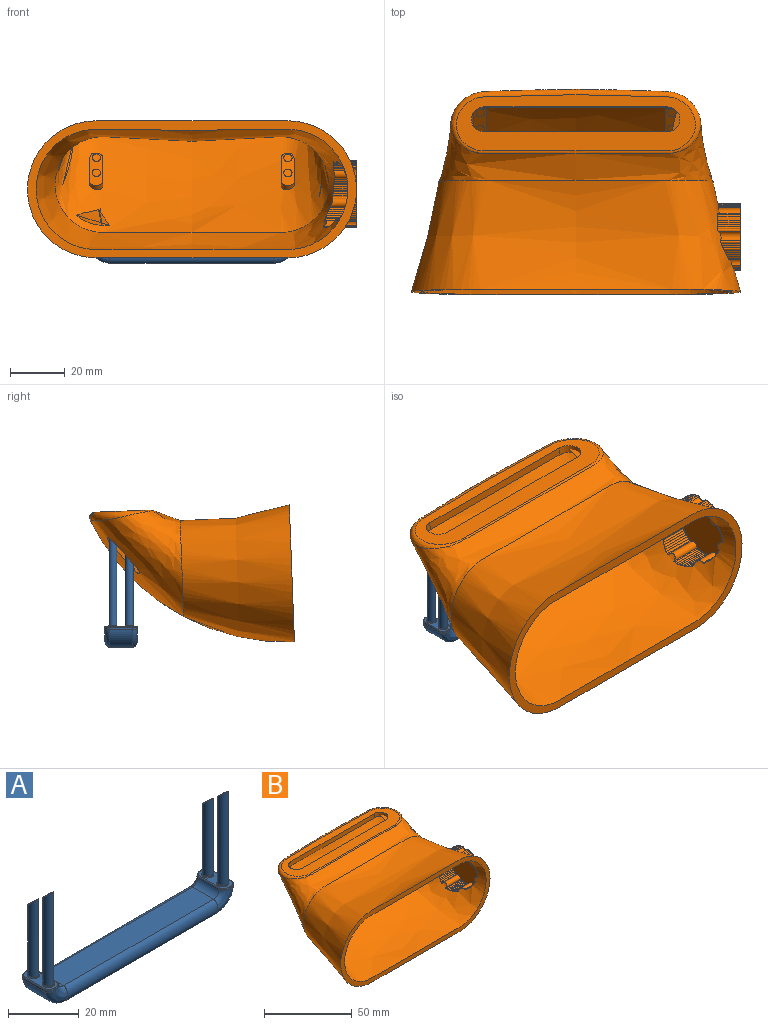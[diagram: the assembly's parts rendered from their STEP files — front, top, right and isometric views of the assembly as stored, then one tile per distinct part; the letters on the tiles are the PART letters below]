
ASSEMBLY  parts=2 mates=1
PART A: 48 faces, bbox 75x15.2x39.8 mm
  f0: cylinder r=1.5mm len=26.61mm, axis (0,0,-1), area 237.6mm2, adj f31,f33
  f1: cylinder r=1.5mm len=32.08mm, axis (0,0,-1), area 289.4mm2, adj f2,f30,f32
  f2: plane 0.1x0mm, normal (0,0,1), area 0mm2, adj f1,f30
  f3: cylinder r=1.5mm len=26.61mm, axis (0,0,-1), area 237.6mm2, adj f29,f41
  f4: cylinder r=1.5mm len=32.08mm, axis (0,0,-1), area 289.4mm2, adj f5,f28,f40
  f5: plane 0.1x0mm, normal (0,0,1), area 0mm2, adj f4,f28
  f6: bspline ~7.5x7.5mm, area 48mm2, adj f9,f10,f13,f23,f25,f37
  f7: bspline ~7.5x7.5mm, area 48mm2, adj f11,f15,f17,f20,f21,f47
  f8: bspline ~7.5x7.5mm, area 48mm2, adj f9,f10,f11,f22,f25,f34
  f9: cylinder r=2.5mm len=8.45mm, axis (0,-1,0), area 31.2mm2, adj f6,f8,f12,f35
  f10: cylinder r=7.5mm len=8.45mm, axis (0,-1,0), area 91mm2, adj f6,f8,f14,f25
  f11: bspline ~60x5mm, area 398.5mm2, adj f7,f8,f12,f14
  f12: plane 60x8.45mm, normal (0,0,1), area 506.7mm2, adj f9,f11,f13,f15
  f13: bspline ~60x5mm, area 398.5mm2, adj f6,f12,f14,f16
  f14: plane 60x8.45mm, normal (0,0,-1), area 506.7mm2, adj f10,f11,f13,f17
  f15: cylinder r=2.5mm len=8.45mm, axis (0,-1,0), area 31.2mm2, adj f7,f12,f16,f45
  f16: bspline ~7.5x7.5mm, area 48mm2, adj f13,f15,f17,f18,f21,f43
  f17: cylinder r=7.5mm len=8.45mm, axis (0,-1,0), area 91mm2, adj f7,f14,f16,f21
  f18: extruded ~2.55x1.69mm, area 2.5mm2, adj f16,f19,f21,f42
  f19: plane 8.45x0.75mm, normal (1,0,0), area 6.3mm2, adj f18,f20,f21,f44
  f20: extruded ~2.55x1.69mm, area 2.5mm2, adj f7,f19,f21,f46
  f21: plane 11.83x2.55mm, normal (0,0,-1), area 0.8mm2, adj f7,f16,f17,f18,f19,f20
  f22: extruded ~2.55x1.69mm, area 2.5mm2, adj f8,f24,f25,f36
  f23: extruded ~2.55x1.69mm, area 2.5mm2, adj f6,f24,f25,f39
  f24: plane 8.45x0.75mm, normal (-1,0,0), area 6.3mm2, adj f22,f23,f25,f38
  f25: plane 11.83x2.55mm, normal (0,0,-1), area 0.8mm2, adj f6,f8,f10,f22,f23,f24
  f26: plane 11.33x4.51mm, normal (0,0,1), area 29mm2, adj f32,f33,f34,f35,f36,f37,f38,f39
  f27: plane 11.33x4.51mm, normal (0,0,1), area 29mm2, adj f40,f41,f42,f43,f44,f45,f46,f47
  f28: plane 3x3mm, normal (0,0.68,0.74), area 9.6mm2, adj f4,f5
  f29: plane 3x3mm, normal (0,0.68,0.74), area 9.6mm2, adj f3
  f30: plane 3x3mm, normal (0,0.68,0.74), area 9.6mm2, adj f1,f2
  f31: plane 3x3mm, normal (0,0.68,0.74), area 9.6mm2, adj f0
  f32: torus R=1.75mm, axis (0,0,-1), area 3.9mm2, adj f1,f26
  f33: torus R=1.75mm, axis (0,0,-1), area 3.9mm2, adj f0,f26
  f34: bspline ~2.86x2.28mm, area 1.2mm2, adj f8,f26,f35,f36
  f35: cylinder r=0.25mm len=8.45mm, axis (0,-1,0), area 3.1mm2, adj f9,f26,f34,f37
  f36: bspline ~2.95x1.97mm, area 1.3mm2, adj f22,f26,f34,f38
  f37: bspline ~2.46x1.69mm, area 1.2mm2, adj f6,f26,f35,f39
  f38: cylinder r=0.25mm len=8.45mm, axis (0,1,0), area 3.3mm2, adj f24,f26,f36,f39
  f39: bspline ~2.69x1.96mm, area 1.3mm2, adj f23,f26,f37,f38
  f40: torus R=1.75mm, axis (0,0,-1), area 3.9mm2, adj f4,f27
  f41: torus R=1.75mm, axis (0,0,-1), area 3.9mm2, adj f3,f27
  f42: bspline ~2.95x1.97mm, area 1.3mm2, adj f18,f27,f43,f44
  f43: bspline ~2.86x2.28mm, area 1.2mm2, adj f16,f27,f42,f45
  f44: cylinder r=0.25mm len=8.45mm, axis (0,-1,0), area 3.3mm2, adj f19,f27,f42,f46
  f45: cylinder r=0.25mm len=8.45mm, axis (0,-1,0), area 3.1mm2, adj f15,f27,f43,f47
  f46: bspline ~2.69x1.96mm, area 1.3mm2, adj f20,f27,f44,f47
  f47: bspline ~2.86x2.28mm, area 1.2mm2, adj f7,f27,f45,f46
PART B: 157 faces, bbox 126x79.2x56 mm
  f0: bspline ~120x50mm, area 10537.9mm2, adj f1,f2,f3,f4,f5,f6,f7,f8
  f1: cylinder r=12mm len=7.29mm, axis (1,0,0), area 0.1mm2, adj f0,f87,f155,f156
  f2: cylinder r=12mm len=7.01mm, axis (1,0,0), area 0.1mm2, adj f0,f87,f154,f155
  f3: cylinder r=12mm len=6.7mm, axis (1,0,0), area 0.1mm2, adj f0,f87,f153,f154
  f4: cylinder r=12mm len=6.36mm, axis (1,0,0), area 0.1mm2, adj f0,f87,f152,f153
  f5: cylinder r=12mm len=6.01mm, axis (1,0,0), area 0.1mm2, adj f0,f87,f151,f152
  f6: cylinder r=12mm len=5.65mm, axis (1,0,0), area 0.1mm2, adj f0,f87,f150,f151
  f7: cylinder r=12mm len=5.28mm, axis (1,0,0), area 0.1mm2, adj f0,f87,f149,f150
  f8: cylinder r=12mm len=4.91mm, axis (1,0,0), area 0.1mm2, adj f0,f87,f148,f149
  f9: cylinder r=12mm len=4.55mm, axis (1,0,0), area 0.1mm2, adj f0,f87,f147,f148
  f10: cylinder r=12mm len=3.02mm, axis (1,0,0), area 0mm2, adj f0,f87,f145,f146
  f11: cylinder r=12mm len=2.81mm, axis (1,0,0), area 0mm2, adj f0,f87,f144,f145
  f12: cylinder r=12mm len=2.63mm, axis (1,0,0), area 0mm2, adj f0,f87,f143,f144
  f13: cylinder r=12mm len=2.49mm, axis (1,0,0), area 0mm2, adj f0,f87,f142,f143
  f14: cylinder r=12mm len=2.4mm, axis (1,0,0), area 0mm2, adj f0,f87,f141,f142
  f15: cylinder r=12mm len=2.36mm, axis (1,0,0), area 0mm2, adj f0,f87,f140,f141
  f16: cylinder r=12mm len=2.36mm, axis (1,0,0), area 0mm2, adj f0,f87,f139,f140
  f17: cylinder r=12mm len=2.41mm, axis (1,0,0), area 0mm2, adj f0,f87,f138,f139
  f18: cylinder r=12mm len=3.42mm, axis (1,0,0), area 0mm2, adj f0,f87,f136,f137
  f19: cylinder r=12mm len=3.76mm, axis (1,0,0), area 0.1mm2, adj f0,f87,f135,f136
  f20: cylinder r=12mm len=4.13mm, axis (1,0,0), area 0.1mm2, adj f0,f87,f134,f135
  f21: cylinder r=12mm len=4.55mm, axis (1,0,0), area 0.1mm2, adj f0,f87,f133,f134
  f22: cylinder r=12mm len=5mm, axis (1,0,0), area 0.1mm2, adj f0,f87,f132,f133
  f23: cylinder r=12mm len=5.47mm, axis (1,0,0), area 0.1mm2, adj f0,f87,f131,f132
  f24: cylinder r=12mm len=5.97mm, axis (1,0,0), area 0.1mm2, adj f0,f87,f130,f131
  f25: cylinder r=12mm len=6.49mm, axis (1,0,0), area 0.1mm2, adj f0,f87,f129,f130
  f26: cylinder r=12mm len=7.01mm, axis (1,0,0), area 0.1mm2, adj f0,f87,f128,f129
  f27: cylinder r=12mm len=9.57mm, axis (1,0,0), area 0.1mm2, adj f0,f87,f126,f127
  f28: cylinder r=12mm len=10.02mm, axis (1,0,0), area 0.1mm2, adj f0,f87,f125,f126
  f29: cylinder r=12mm len=10.43mm, axis (1,0,0), area 0.1mm2, adj f0,f87,f124,f125
  f30: cylinder r=12mm len=10.79mm, axis (1,0,0), area 0.1mm2, adj f0,f87,f123,f124
  f31: cylinder r=12mm len=11.11mm, axis (1,0,0), area 0.2mm2, adj f0,f87,f122,f123
  f32: cylinder r=12mm len=11.38mm, axis (1,0,0), area 0.2mm2, adj f0,f87,f121,f122
  f33: cylinder r=12mm len=11.59mm, axis (1,0,0), area 0.2mm2, adj f0,f87,f120,f121
  f34: cylinder r=12mm len=11.74mm, axis (1,0,0), area 0.2mm2, adj f0,f87,f119,f120
  f35: cylinder r=12mm len=11.67mm, axis (1,0,0), area 0.2mm2, adj f0,f87,f117,f118
  f36: cylinder r=12mm len=11.51mm, axis (1,0,0), area 0.2mm2, adj f0,f87,f116,f117
  f37: cylinder r=12mm len=11.31mm, axis (1,0,0), area 0.2mm2, adj f0,f87,f115,f116
  f38: cylinder r=12mm len=11.09mm, axis (1,0,0), area 0.2mm2, adj f0,f87,f114,f115
  f39: cylinder r=12mm len=10.85mm, axis (1,0,0), area 0.2mm2, adj f0,f87,f113,f114
  f40: cylinder r=12mm len=10.59mm, axis (1,0,0), area 0.1mm2, adj f0,f87,f112,f113
  f41: cylinder r=12mm len=10.32mm, axis (1,0,0), area 0.1mm2, adj f0,f87,f111,f112
  f42: cylinder r=12mm len=10.05mm, axis (1,0,0), area 0.1mm2, adj f0,f87,f110,f111
  f43: cylinder r=12mm len=9.79mm, axis (1,0,0), area 0.1mm2, adj f0,f87,f109,f110
  f44: cylinder r=12mm len=8.87mm, axis (1,0,0), area 0.1mm2, adj f0,f87,f107,f108
  f45: cylinder r=12mm len=8.69mm, axis (1,0,0), area 0.1mm2, adj f0,f87,f106,f107
  f46: cylinder r=12mm len=8.53mm, axis (1,0,0), area 0.1mm2, adj f0,f87,f105,f106
  f47: cylinder r=12mm len=8.41mm, axis (1,0,0), area 0.1mm2, adj f0,f87,f104,f105
  f48: cylinder r=12mm len=8.3mm, axis (1,0,0), area 0.1mm2, adj f0,f87,f103,f104
  f49: cylinder r=12mm len=8.23mm, axis (1,0,0), area 0.1mm2, adj f0,f87,f102,f103
  f50: cylinder r=12mm len=8.18mm, axis (1,0,0), area 0.1mm2, adj f0,f87,f101,f102
  f51: cylinder r=12mm len=8.15mm, axis (1,0,0), area 0.1mm2, adj f0,f87,f100,f101
  f52: cylinder r=12mm len=8.14mm, axis (1,0,0), area 0.1mm2, adj f0,f87,f99,f100
  f53: cylinder r=12mm len=8.29mm, axis (1,0,0), area 0.1mm2, adj f0,f87,f97,f98
  f54: cylinder r=12mm len=8.33mm, axis (1,0,0), area 0.1mm2, adj f0,f87,f96,f97
  f55: cylinder r=12mm len=8.36mm, axis (1,0,0), area 0.1mm2, adj f0,f87,f95,f96
  f56: cylinder r=12mm len=8.38mm, axis (1,0,0), area 0.1mm2, adj f0,f87,f94,f95
  f57: cylinder r=12mm len=8.38mm, axis (1,0,0), area 0.1mm2, adj f0,f87,f93,f94
  f58: cylinder r=12mm len=8.35mm, axis (1,0,0), area 0.1mm2, adj f0,f87,f92,f93
  f59: cylinder r=12mm len=8.3mm, axis (1,0,0), area 0.1mm2, adj f0,f87,f91,f92
  f60: cylinder r=12mm len=8.22mm, axis (1,0,0), area 0.1mm2, adj f0,f87,f90,f91
  f61: plane 87.25x20.53mm, normal (0,0,1), area 995.7mm2, adj f67,f78,f79,f80,f81
  f62: plane 86.4x19.72mm, normal (0,0,-1), area 803.8mm2, adj f65,f78,f79,f80,f81
  f63: bspline ~99.89x39.05mm, area 6088.6mm2, adj f0,f67,f68,f69,f70,f71,f72,f73
  f64: plane 122.15x52.15mm, normal (0,-1,0), area 890.7mm2, adj f0,f66
  f65: offset ~106.46x46.36mm, area 5444.4mm2, adj f62,f66
  f66: offset ~125.38x55.93mm, area 9925.7mm2, adj f64,f65
  f67: bspline ~90.94x23.42mm, area 539.5mm2, adj f61,f63
  f68: plane 10.48x9.69mm, normal (1,0,0), area 21.5mm2, adj f63,f69,f71,f72
  f69: cylinder r=2.5mm len=4.05mm, axis (0,-0.7,0.71), area 2.9mm2, adj f63,f68,f72
  f70: plane 8.92x8.26mm, normal (-1,0,0), area 6.5mm2, adj f63,f71,f72
  f71: cylinder r=2.5mm len=5mm, axis (0,-0.7,0.71), area 13.2mm2, adj f63,f68,f70,f72
  f72: plane 12.53x12.38mm, normal (0,0.7,-0.71), area 81.4mm2, adj f63,f68,f69,f70,f71
  f73: plane 9.13x8.45mm, normal (1,0,0), area 6.8mm2, adj f63,f76,f77
  f74: cylinder r=2.5mm len=4.22mm, axis (0,-0.7,0.71), area 3mm2, adj f63,f75,f77
  f75: plane 10.49x9.7mm, normal (-1,0,0), area 21.6mm2, adj f63,f74,f76,f77
  f76: cylinder r=2.5mm len=5mm, axis (0,-0.7,0.71), area 13.2mm2, adj f63,f73,f75,f77
  f77: plane 12.5x12.36mm, normal (0,0.7,-0.71), area 81.7mm2, adj f63,f73,f74,f75,f76
  f78: plane 67x3mm, normal (0,-1,0), area 201mm2, adj f61,f62,f79,f81
  f79: cylinder r=4.5mm len=9mm, axis (0,0,1), area 42.4mm2, adj f61,f62,f78,f80
  f80: plane 67x3mm, normal (0,1,0), area 201mm2, adj f61,f62,f79,f81
  f81: cylinder r=4.5mm len=9mm, axis (0,0,1), area 42.4mm2, adj f61,f62,f78,f80
  f82: cylinder r=1.75mm len=4.43mm, axis (1,0,0), area 17.7mm2, adj f0,f87,f146,f147
  f83: cylinder r=1.75mm len=3.31mm, axis (1,0,0), area 13.2mm2, adj f0,f87,f137,f138
  f84: cylinder r=1.75mm len=9.18mm, axis (1,0,0), area 37mm2, adj f0,f87,f127,f128
  f85: cylinder r=1.75mm len=12.01mm, axis (1,0,0), area 56.1mm2, adj f0,f87,f118,f119
  f86: cylinder r=1.75mm len=9.8mm, axis (1,0,0), area 41.2mm2, adj f0,f87,f108,f109
  f87: plane 24.46x24.29mm, normal (1,0,0), area 440.1mm2, adj f1,f2,f3,f4,f5,f6,f7,f8
  f88: cylinder r=1.75mm len=8.11mm, axis (1,0,0), area 34.1mm2, adj f0,f87,f90,f156
  f89: cylinder r=1.75mm len=8.34mm, axis (1,0,0), area 38.9mm2, adj f0,f87,f98,f99
  f90: cylinder r=0.5mm len=8.22mm, axis (1,0,0), area 8.3mm2, adj f0,f60,f87,f88
  f91: cylinder r=0.5mm len=8.3mm, axis (1,0,0), area 8.4mm2, adj f0,f59,f60,f87
  f92: cylinder r=0.5mm len=8.35mm, axis (1,0,0), area 8.5mm2, adj f0,f58,f59,f87
  f93: cylinder r=0.5mm len=8.38mm, axis (1,0,0), area 8.5mm2, adj f0,f57,f58,f87
  f94: cylinder r=0.5mm len=8.38mm, axis (1,0,0), area 8.6mm2, adj f0,f56,f57,f87
  f95: cylinder r=0.5mm len=8.38mm, axis (1,0,0), area 8.5mm2, adj f0,f55,f56,f87
  f96: cylinder r=0.5mm len=8.36mm, axis (1,0,0), area 8.5mm2, adj f0,f54,f55,f87
  f97: cylinder r=0.5mm len=8.33mm, axis (1,0,0), area 8.5mm2, adj f0,f53,f54,f87
  f98: cylinder r=0.5mm len=8.34mm, axis (1,0,0), area 5mm2, adj f0,f53,f87,f89
  f99: cylinder r=0.5mm len=8.2mm, axis (1,0,0), area 4.3mm2, adj f0,f52,f87,f89
  f100: cylinder r=0.5mm len=8.15mm, axis (1,0,0), area 8.3mm2, adj f0,f51,f52,f87
  f101: cylinder r=0.5mm len=8.17mm, axis (1,0,0), area 8.3mm2, adj f0,f50,f51,f87
  f102: cylinder r=0.5mm len=8.23mm, axis (1,0,0), area 8.4mm2, adj f0,f49,f50,f87
  f103: cylinder r=0.5mm len=8.3mm, axis (1,0,0), area 8.4mm2, adj f0,f48,f49,f87
  f104: cylinder r=0.5mm len=8.4mm, axis (1,0,0), area 8.5mm2, adj f0,f47,f48,f87
  f105: cylinder r=0.5mm len=8.53mm, axis (1,0,0), area 8.6mm2, adj f0,f46,f47,f87
  f106: cylinder r=0.5mm len=8.69mm, axis (1,0,0), area 8.8mm2, adj f0,f45,f46,f87
  f107: cylinder r=0.5mm len=8.86mm, axis (1,0,0), area 9mm2, adj f0,f44,f45,f87
  f108: cylinder r=0.5mm len=8.89mm, axis (1,0,0), area 0.6mm2, adj f0,f44,f86,f87
  f109: cylinder r=0.5mm len=9.8mm, axis (1,0,0), area 1.4mm2, adj f0,f43,f86,f87
  f110: cylinder r=0.5mm len=10.05mm, axis (1,0,0), area 10.1mm2, adj f0,f42,f43,f87
  f111: cylinder r=0.5mm len=10.32mm, axis (1,0,0), area 10.4mm2, adj f0,f41,f42,f87
  f112: cylinder r=0.5mm len=10.58mm, axis (1,0,0), area 10.7mm2, adj f0,f40,f41,f87
  f113: cylinder r=0.5mm len=10.84mm, axis (1,0,0), area 10.9mm2, adj f0,f39,f40,f87
  f114: cylinder r=0.5mm len=11.09mm, axis (1,0,0), area 11.2mm2, adj f0,f38,f39,f87
  f115: cylinder r=0.5mm len=11.31mm, axis (1,0,0), area 11.4mm2, adj f0,f37,f38,f87
  f116: cylinder r=0.5mm len=11.5mm, axis (1,0,0), area 11.6mm2, adj f0,f36,f37,f87
  f117: cylinder r=0.5mm len=11.66mm, axis (1,0,0), area 11.8mm2, adj f0,f35,f36,f87
  f118: cylinder r=0.5mm len=11.92mm, axis (1,0,0), area 5.6mm2, adj f0,f35,f85,f87
  f119: cylinder r=0.5mm len=12.01mm, axis (1,0,0), area 7.8mm2, adj f0,f34,f85,f87
  f120: cylinder r=0.5mm len=11.74mm, axis (1,0,0), area 11.9mm2, adj f0,f33,f34,f87
  f121: cylinder r=0.5mm len=11.59mm, axis (1,0,0), area 11.7mm2, adj f0,f32,f33,f87
  f122: cylinder r=0.5mm len=11.38mm, axis (1,0,0), area 11.5mm2, adj f0,f31,f32,f87
  f123: cylinder r=0.5mm len=11.11mm, axis (1,0,0), area 11.2mm2, adj f0,f30,f31,f87
  f124: cylinder r=0.5mm len=10.79mm, axis (1,0,0), area 10.8mm2, adj f0,f29,f30,f87
  f125: cylinder r=0.5mm len=10.42mm, axis (1,0,0), area 10.4mm2, adj f0,f28,f29,f87
  f126: cylinder r=0.5mm len=10.01mm, axis (1,0,0), area 10mm2, adj f0,f27,f28,f87
  f127: cylinder r=0.5mm len=9.56mm, axis (1,0,0), area 8.5mm2, adj f0,f27,f84,f87
  f128: cylinder r=0.5mm len=7.19mm, axis (1,0,0), area 2mm2, adj f0,f26,f84,f87
  f129: cylinder r=0.5mm len=7mm, axis (1,0,0), area 6.9mm2, adj f0,f25,f26,f87
  f130: cylinder r=0.5mm len=6.48mm, axis (1,0,0), area 6.4mm2, adj f0,f24,f25,f87
  f131: cylinder r=0.5mm len=5.96mm, axis (1,0,0), area 5.8mm2, adj f0,f23,f24,f87
  f132: cylinder r=0.5mm len=5.47mm, axis (1,0,0), area 5.3mm2, adj f0,f22,f23,f87
  f133: cylinder r=0.5mm len=4.99mm, axis (1,0,0), area 4.9mm2, adj f0,f21,f22,f87
  f134: cylinder r=0.5mm len=4.54mm, axis (1,0,0), area 4.4mm2, adj f0,f20,f21,f87
  f135: cylinder r=0.5mm len=4.13mm, axis (1,0,0), area 4mm2, adj f0,f19,f20,f87
  f136: cylinder r=0.5mm len=3.75mm, axis (1,0,0), area 3.7mm2, adj f0,f18,f19,f87
  f137: cylinder r=0.5mm len=3.41mm, axis (1,0,0), area 1.2mm2, adj f0,f18,f83,f87
  f138: cylinder r=0.5mm len=2.45mm, axis (1,0,0), area 2mm2, adj f0,f17,f83,f87
  f139: cylinder r=0.5mm len=2.41mm, axis (1,0,0), area 2.4mm2, adj f0,f16,f17,f87
  f140: cylinder r=0.5mm len=2.36mm, axis (1,0,0), area 2.4mm2, adj f0,f15,f16,f87
  f141: cylinder r=0.5mm len=2.4mm, axis (1,0,0), area 2.4mm2, adj f0,f14,f15,f87
  f142: cylinder r=0.5mm len=2.49mm, axis (1,0,0), area 2.5mm2, adj f0,f13,f14,f87
  f143: cylinder r=0.5mm len=2.63mm, axis (1,0,0), area 2.6mm2, adj f0,f12,f13,f87
  f144: cylinder r=0.5mm len=2.8mm, axis (1,0,0), area 2.8mm2, adj f0,f11,f12,f87
  f145: cylinder r=0.5mm len=3.02mm, axis (1,0,0), area 3mm2, adj f0,f10,f11,f87
  f146: cylinder r=0.5mm len=3.18mm, axis (1,0,0), area 2.3mm2, adj f0,f10,f82,f87
  f147: cylinder r=0.5mm len=4.55mm, axis (1,0,0), area 1.8mm2, adj f0,f9,f82,f87
  f148: cylinder r=0.5mm len=4.91mm, axis (1,0,0), area 4.8mm2, adj f0,f8,f9,f87
  f149: cylinder r=0.5mm len=5.28mm, axis (1,0,0), area 5.2mm2, adj f0,f7,f8,f87
  f150: cylinder r=0.5mm len=5.64mm, axis (1,0,0), area 5.6mm2, adj f0,f6,f7,f87
  f151: cylinder r=0.5mm len=6.01mm, axis (1,0,0), area 5.9mm2, adj f0,f5,f6,f87
  f152: cylinder r=0.5mm len=6.36mm, axis (1,0,0), area 6.3mm2, adj f0,f4,f5,f87
  f153: cylinder r=0.5mm len=6.69mm, axis (1,0,0), area 6.7mm2, adj f0,f3,f4,f87
  f154: cylinder r=0.5mm len=7mm, axis (1,0,0), area 7mm2, adj f0,f2,f3,f87
  f155: cylinder r=0.5mm len=7.29mm, axis (1,0,0), area 7.3mm2, adj f0,f1,f2,f87
  f156: cylinder r=0.5mm len=7.41mm, axis (1,0,0), area 1.6mm2, adj f0,f1,f87,f88
PLACE A rot(axis=(0,0,1),180deg) t=(-69.98,150.42,-1.2)mm
PLACE B rot(axis=(-1,0,0),2.2deg) t=(-70.72,78.54,32.91)mm
MATE fastened B.f69 <-> A.f30  axis (0,0.68,-0.74) through (-35.72,144.78,69.43)mm
